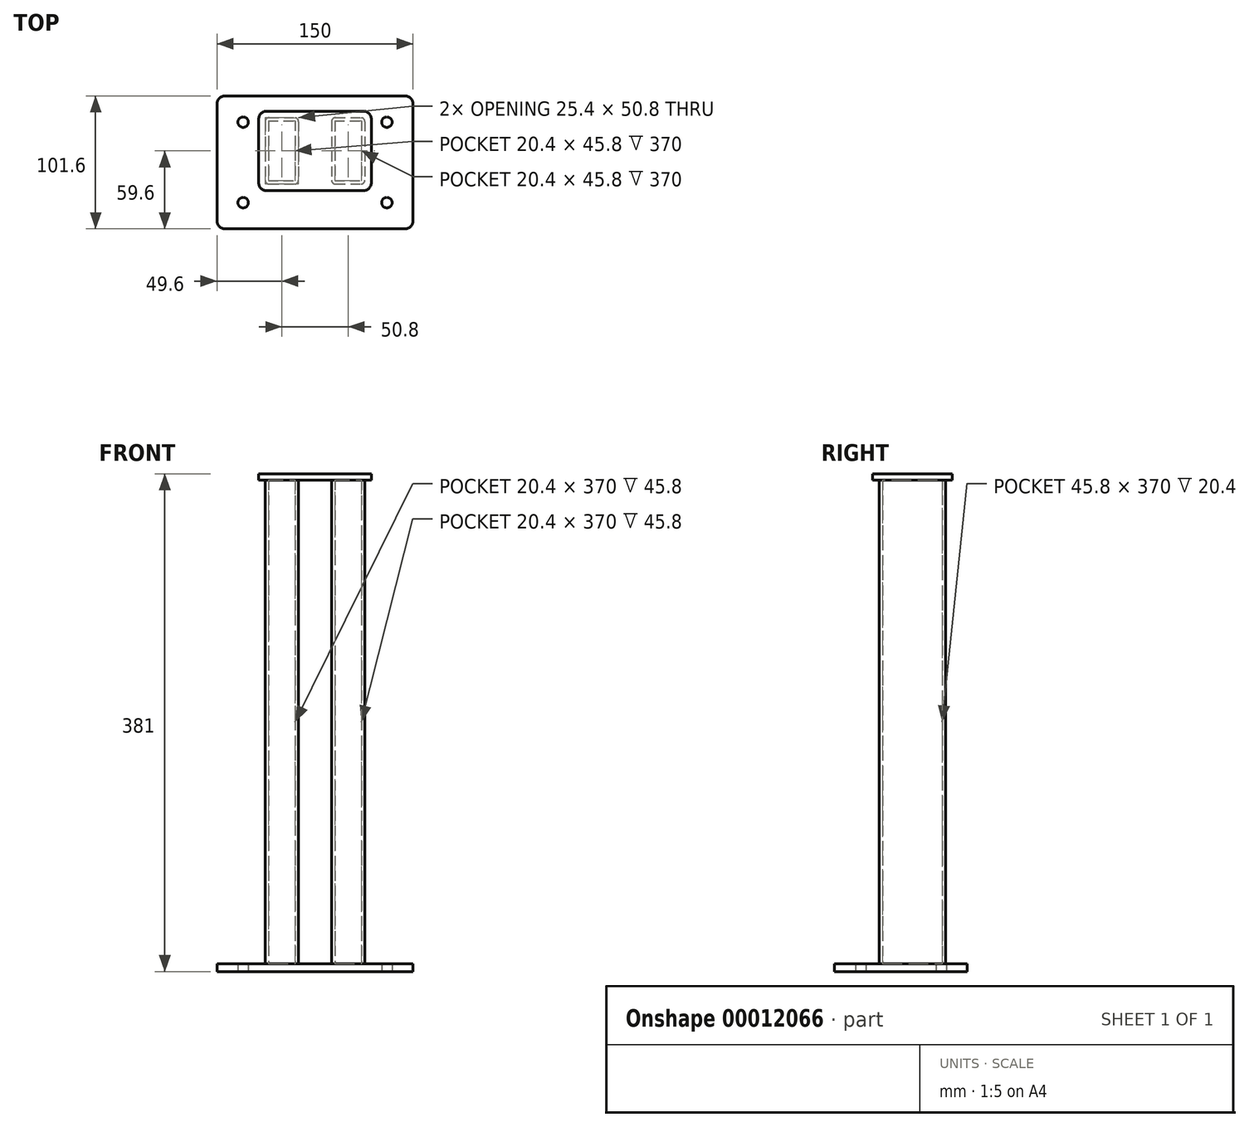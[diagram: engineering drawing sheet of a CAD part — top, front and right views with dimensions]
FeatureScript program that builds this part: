
annotation { "Feature Type Name" : "Feature", "Feature Type Description" : "" }
export const myFeature = defineFeature(function(context is Context, id is Id, definition is map)
    precondition{}
    {
        {
            var Q0;
            Q0=qCreatedBy(makeId("Top.planeOp"),FACE);
            var sketch = newSketch(context, id + "F0", { "sketchPlane" : qUnion([Q0])});
            skLineSegment(sketch, "E0.bottom", {"start": v(6, 0) * mm, "end": v(144, 0) * mm});
            skLineSegment(sketch, "E0.top", {"start": v(6, 101.6) * mm, "end": v(144, 101.6) * mm});
            skLineSegment(sketch, "E0.left", {"start": v(0, 6) * mm, "end": v(0, 95.6) * mm});
            skLineSegment(sketch, "E0.right", {"start": v(150, 6) * mm, "end": v(150, 95.6) * mm});
            skCircle(sketch, "E1", {"center": v(20, 20) * mm, "radius": 4 * mm});
            skCircle(sketch, "E2", {"center": v(130, 20) * mm, "radius": 4 * mm});
            skCircle(sketch, "E3", {"center": v(130, 81.6) * mm, "radius": 4 * mm});
            skCircle(sketch, "E4", {"center": v(20, 81.6) * mm, "radius": 4 * mm});
            skPoint(sketch, "E5.visualSharp", {"position": v(0, 0) * mm});
            skArc(sketch, "E5.filletArc", {"start": v(0, 6) * mm, "mid": v(1.76, 1.76) * mm, "end": v(6, 0) * mm});
            skPoint(sketch, "E6.visualSharp", {"position": v(150, 0) * mm});
            skArc(sketch, "E6.filletArc", {"start": v(144, 0) * mm, "mid": v(148.24, 1.76) * mm, "end": v(150, 6) * mm});
            skPoint(sketch, "E7.visualSharp", {"position": v(150, 101.6) * mm});
            skArc(sketch, "E7.filletArc", {"start": v(150, 95.6) * mm, "mid": v(148.24, 99.84) * mm, "end": v(144, 101.6) * mm});
            skPoint(sketch, "E8.visualSharp", {"position": v(0, 101.6) * mm});
            skArc(sketch, "E8.filletArc", {"start": v(6, 101.6) * mm, "mid": v(1.76, 99.84) * mm, "end": v(0, 95.6) * mm});
            skSolve(sketch);
        }
        {
            var Q0;
            Q0 = qSketchRegion(id + "F0", true);
            extrude(context, id + "F1", {"entities" : qUnion([Q0]), "depth" : 6 * mm});
        }
        {
            var Q0;
            Q0=makeQuery(id+"F1.opExtrude","CAP_FACE",FACE,{"disambiguationData":[OSD([sQuery(id+"F0.wireOp",EDGE,"E0.bottom"),sQuery(id+"F0.wireOp",EDGE,"E0.top"),sQuery(id+"F0.wireOp",EDGE,"E0.left"),sQuery(id+"F0.wireOp",EDGE,"E0.right")])],"isStart":false});
            var sketch = newSketch(context, id + "F2", { "sketchPlane" : qUnion([Q0])});
            skLineSegment(sketch, "E9.0", {"start": v(62.3, 82) * mm, "end": v(62.3, 37.2) * mm});
            skLineSegment(sketch, "E10.0", {"start": v(87.7, 82) * mm, "end": v(87.7, 37.2) * mm});
            skLineSegment(sketch, "E11.0", {"start": v(36.9, 82) * mm, "end": v(36.9, 37.2) * mm});
            skLineSegment(sketch, "E12.0", {"start": v(113.1, 82) * mm, "end": v(113.1, 37.2) * mm});
            skLineSegment(sketch, "E13.0", {"start": v(39.9, 85) * mm, "end": v(59.3, 85) * mm});
            skLineSegment(sketch, "E14.0", {"start": v(39.9, 34.2) * mm, "end": v(59.3, 34.2) * mm});
            skLineSegment(sketch, "E15.trimOffspring", {"start": v(90.7, 85) * mm, "end": v(110.1, 85) * mm});
            skLineSegment(sketch, "E16.trimOffspring", {"start": v(90.7, 34.2) * mm, "end": v(110.1, 34.2) * mm});
            skPoint(sketch, "E17.end.orphan", {"position": v(75, 0) * mm});
            skPoint(sketch, "E17.start.orphan", {"position": v(75, 100) * mm});
            skPoint(sketch, "E18.visualSharp", {"position": v(36.9, 85) * mm});
            skArc(sketch, "E18.filletArc", {"start": v(39.9, 85) * mm, "mid": v(37.78, 84.12) * mm, "end": v(36.9, 82) * mm});
            skPoint(sketch, "E19.visualSharp", {"position": v(62.3, 85) * mm});
            skArc(sketch, "E19.filletArc", {"start": v(62.3, 82) * mm, "mid": v(61.42, 84.12) * mm, "end": v(59.3, 85) * mm});
            skPoint(sketch, "E20.visualSharp", {"position": v(62.3, 34.2) * mm});
            skArc(sketch, "E20.filletArc", {"start": v(59.3, 34.2) * mm, "mid": v(61.42, 35.08) * mm, "end": v(62.3, 37.2) * mm});
            skPoint(sketch, "E21.visualSharp", {"position": v(36.9, 34.2) * mm});
            skArc(sketch, "E21.filletArc", {"start": v(36.9, 37.2) * mm, "mid": v(37.78, 35.08) * mm, "end": v(39.9, 34.2) * mm});
            skPoint(sketch, "E22.visualSharp", {"position": v(87.7, 34.2) * mm});
            skArc(sketch, "E22.filletArc", {"start": v(87.7, 37.2) * mm, "mid": v(88.58, 35.08) * mm, "end": v(90.7, 34.2) * mm});
            skPoint(sketch, "E23.visualSharp", {"position": v(113.1, 34.2) * mm});
            skArc(sketch, "E23.filletArc", {"start": v(110.1, 34.2) * mm, "mid": v(112.22, 35.08) * mm, "end": v(113.1, 37.2) * mm});
            skPoint(sketch, "E24.visualSharp", {"position": v(113.1, 85) * mm});
            skArc(sketch, "E24.filletArc", {"start": v(113.1, 82) * mm, "mid": v(112.22, 84.12) * mm, "end": v(110.1, 85) * mm});
            skPoint(sketch, "E25.visualSharp", {"position": v(87.7, 85) * mm});
            skArc(sketch, "E25.filletArc", {"start": v(90.7, 85) * mm, "mid": v(88.58, 84.12) * mm, "end": v(87.7, 82) * mm});
            skLineSegment(sketch, "E26.0", {"start": v(39.4, 82.5) * mm, "end": v(39.4, 36.7) * mm});
            skLineSegment(sketch, "E26.1", {"start": v(39.4, 82.5) * mm, "end": v(59.8, 82.5) * mm});
            skLineSegment(sketch, "E26.2", {"start": v(59.8, 82.5) * mm, "end": v(59.8, 36.7) * mm});
            skLineSegment(sketch, "E26.3", {"start": v(39.4, 36.7) * mm, "end": v(59.8, 36.7) * mm});
            skLineSegment(sketch, "E27.0", {"start": v(90.2, 82.5) * mm, "end": v(110.6, 82.5) * mm});
            skLineSegment(sketch, "E27.1", {"start": v(90.2, 82.5) * mm, "end": v(90.2, 36.7) * mm});
            skLineSegment(sketch, "E27.2", {"start": v(90.2, 36.7) * mm, "end": v(110.6, 36.7) * mm});
            skLineSegment(sketch, "E27.3", {"start": v(110.6, 82.5) * mm, "end": v(110.6, 36.7) * mm});
            skSolve(sketch);
        }
        {
            var Q0;
            Q0 = qSketchRegion(id + "F2", true);
            extrude(context, id + "F3", {"entities" : qUnion([Q0]), "operationType" : NewBodyOperationType.ADD, "depth" : 370 * mm});
        }
        {
            var Q0;
            Q0=makeQuery(id+"F3.opExtrude","CAP_FACE",FACE,{"disambiguationData":[OSD([sQuery(id+"F2.wireOp",EDGE,"E9.0"),sQuery(id+"F2.wireOp",EDGE,"E11.0"),sQuery(id+"F2.wireOp",EDGE,"E13.0"),sQuery(id+"F2.wireOp",EDGE,"E14.0"),sQuery(id+"F2.wireOp",EDGE,"E18.filletArc"),sQuery(id+"F2.wireOp",EDGE,"E19.filletArc"),sQuery(id+"F2.wireOp",EDGE,"E20.filletArc"),sQuery(id+"F2.wireOp",EDGE,"E21.filletArc"),sQuery(id+"F2.wireOp",EDGE,"E26.0"),sQuery(id+"F2.wireOp",EDGE,"E26.1"),sQuery(id+"F2.wireOp",EDGE,"E26.2"),sQuery(id+"F2.wireOp",EDGE,"E26.3")])],"isStart":false});
            var sketch = newSketch(context, id + "F4", { "sketchPlane" : qUnion([Q0])});
            skLineSegment(sketch, "E28.0", {"start": v(31.9, 84) * mm, "end": v(31.9, 35.2) * mm});
            skLineSegment(sketch, "E29.0", {"start": v(37.9, 90) * mm, "end": v(112.1, 90) * mm});
            skLineSegment(sketch, "E30.0", {"start": v(118.1, 84) * mm, "end": v(118.1, 35.2) * mm});
            skLineSegment(sketch, "E31.0", {"start": v(37.9, 29.2) * mm, "end": v(112.1, 29.2) * mm});
            skPoint(sketch, "E32.visualSharp", {"position": v(31.9, 29.2) * mm});
            skArc(sketch, "E32.filletArc", {"start": v(31.9, 35.2) * mm, "mid": v(33.66, 30.96) * mm, "end": v(37.9, 29.2) * mm});
            skPoint(sketch, "E33.visualSharp", {"position": v(31.9, 90) * mm});
            skArc(sketch, "E33.filletArc", {"start": v(37.9, 90) * mm, "mid": v(33.66, 88.24) * mm, "end": v(31.9, 84) * mm});
            skPoint(sketch, "E34.visualSharp", {"position": v(118.1, 90) * mm});
            skArc(sketch, "E34.filletArc", {"start": v(118.1, 84) * mm, "mid": v(116.34, 88.24) * mm, "end": v(112.1, 90) * mm});
            skPoint(sketch, "E35.visualSharp", {"position": v(118.1, 29.2) * mm});
            skArc(sketch, "E35.filletArc", {"start": v(112.1, 29.2) * mm, "mid": v(116.34, 30.96) * mm, "end": v(118.1, 35.2) * mm});
            skSolve(sketch);
        }
        {
            var Q0;
            Q0 = qSketchRegion(id + "F4", true);
            extrude(context, id + "F5", {"entities" : qUnion([Q0]), "operationType" : NewBodyOperationType.ADD, "depth" : 5 * mm});
        }
    });
